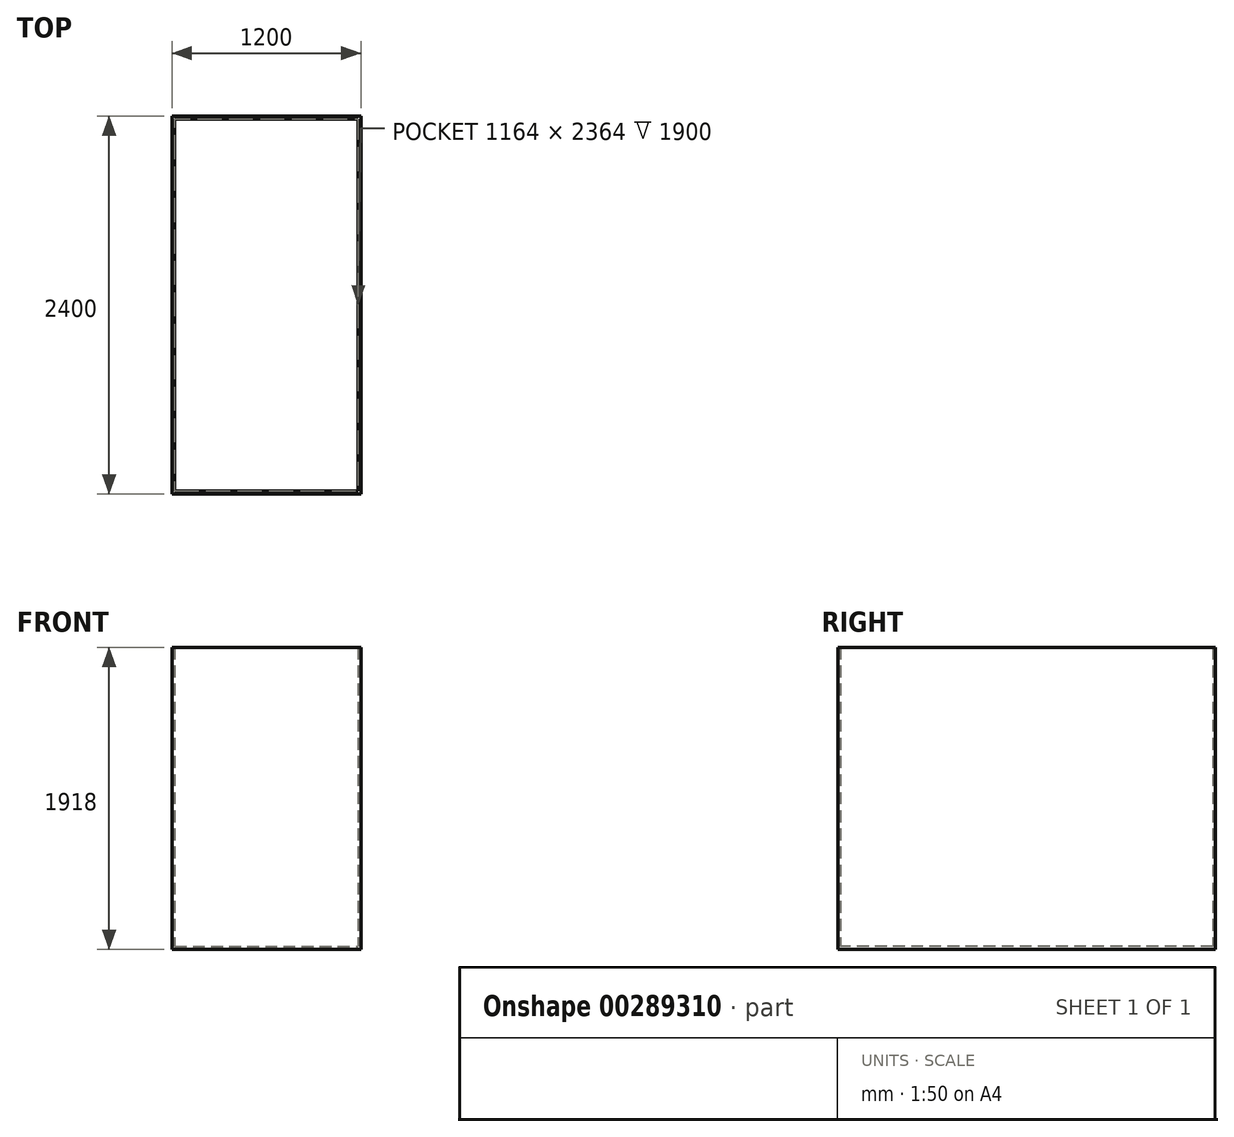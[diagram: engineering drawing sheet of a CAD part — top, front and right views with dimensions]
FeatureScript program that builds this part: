
annotation { "Feature Type Name" : "Feature", "Feature Type Description" : "" }
export const myFeature = defineFeature(function(context is Context, id is Id, definition is map)
    precondition{}
    {
        {
            var Q0;
            Q0=qCreatedBy(makeId("Top.planeOp"),FACE);
            var sketch = newSketch(context, id + "F0", { "sketchPlane" : qUnion([Q0])});
            skLineSegment(sketch, "E0.bottom", {"start": v(-578.5, 1685.17) * mm, "end": v(621.5, 1685.17) * mm});
            skLineSegment(sketch, "E0.top", {"start": v(-578.5, -714.83) * mm, "end": v(621.5, -714.83) * mm});
            skLineSegment(sketch, "E0.left", {"start": v(-578.5, 1685.17) * mm, "end": v(-578.5, -714.83) * mm});
            skLineSegment(sketch, "E0.right", {"start": v(621.5, 1685.17) * mm, "end": v(621.5, -714.83) * mm});
            skLineSegment(sketch, "E1.0", {"start": v(-560.5, 1667.17) * mm, "end": v(603.5, 1667.17) * mm});
            skLineSegment(sketch, "E1.1", {"start": v(-560.5, 1667.17) * mm, "end": v(-560.5, -696.83) * mm});
            skLineSegment(sketch, "E1.2", {"start": v(-560.5, -696.83) * mm, "end": v(603.5, -696.83) * mm});
            skLineSegment(sketch, "E1.3", {"start": v(603.5, 1667.17) * mm, "end": v(603.5, -696.83) * mm});
            skSolve(sketch);
        }
        {
            var Q0;
            Q0=makeQuery(id+"F0.imprint","IMPRINT",FACE,{"disambiguationData":[TD([[makeQuery(id+"F0.imprint","IMPRINT",EDGE,{"derivedFrom":sQuery(id+"F0.wireOp",EDGE,"E1.0")}),-1.0]])]});
            var Q1;
            Q1=makeQuery(id+"F0.imprint","IMPRINT",FACE,{"disambiguationData":[TD([[makeQuery(id+"F0.imprint","IMPRINT",EDGE,{"derivedFrom":sQuery(id+"F0.wireOp",EDGE,"E0.bottom")}),-1.0]])]});
            extrude(context, id + "F1", {"entities" : qUnion([Q0, Q1]), "oppositeDirection" : true, "depth" : 18 * mm});
        }
        {
            var Q0;
            Q0 = qSketchRegion(id + "F0", true);
            extrude(context, id + "F2", {"entities" : qUnion([Q0]), "operationType" : NewBodyOperationType.ADD, "depth" : 1900 * mm});
        }
    });
